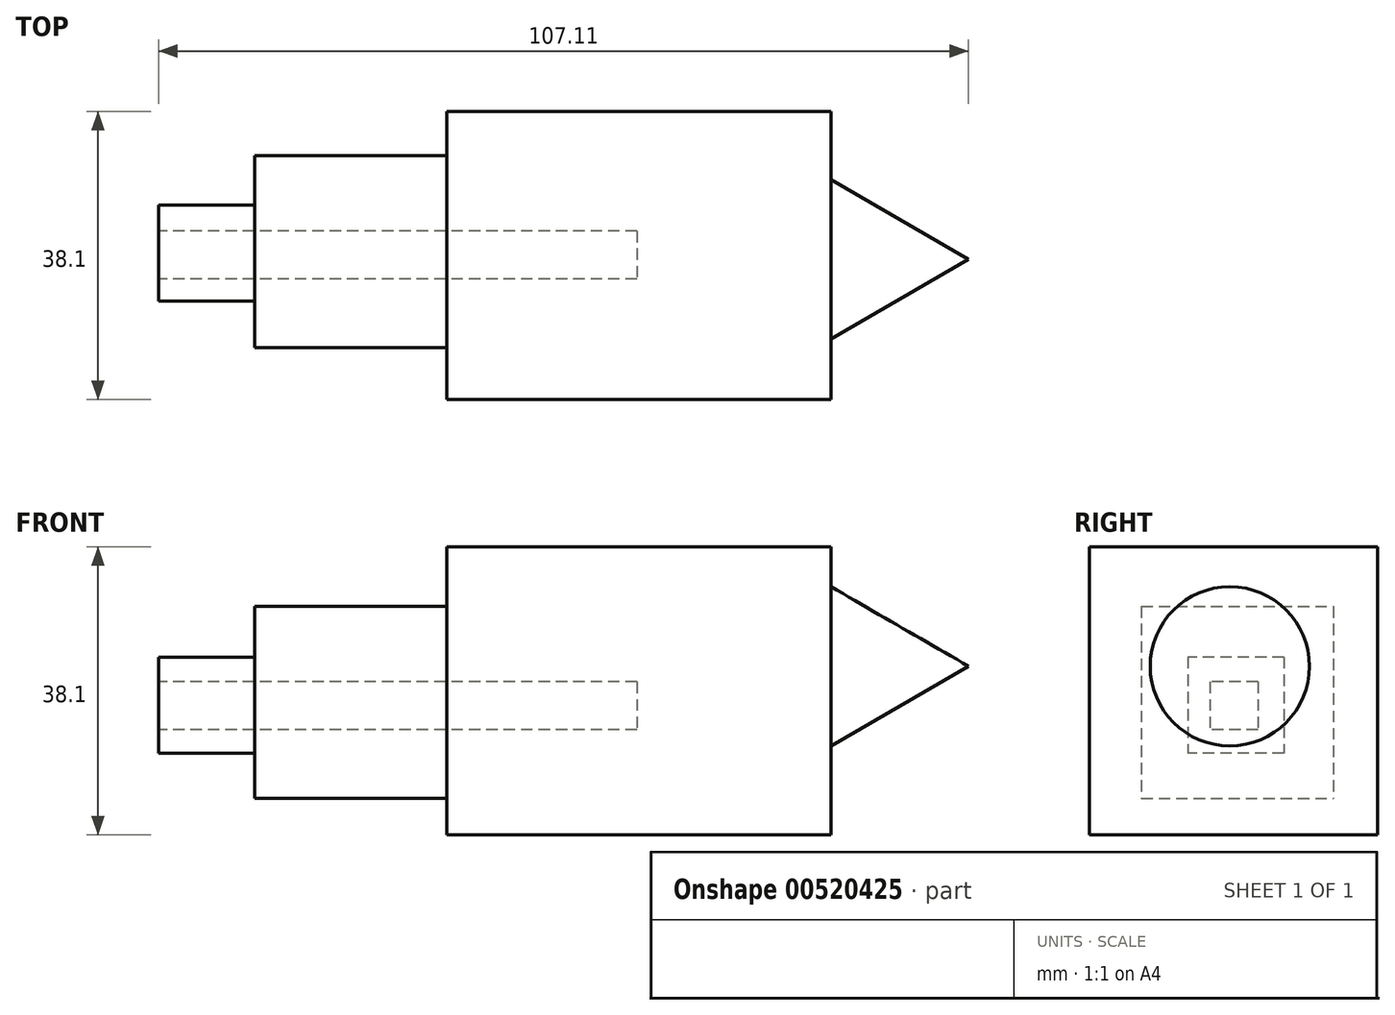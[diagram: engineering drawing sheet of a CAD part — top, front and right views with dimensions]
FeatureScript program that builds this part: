
annotation { "Feature Type Name" : "Feature", "Feature Type Description" : "" }
export const myFeature = defineFeature(function(context is Context, id is Id, definition is map)
    precondition{}
    {
        {
            var Q0;
            Q0=qCreatedBy(makeId("Right.planeOp"),FACE);
            var sketch = newSketch(context, id + "F0", { "sketchPlane" : qUnion([Q0])});
            skLineSegment(sketch, "E0.bottom", {"start": v(-18.66, 15.8) * mm, "end": v(19.44, 15.8) * mm});
            skLineSegment(sketch, "E0.top", {"start": v(-18.66, -22.3) * mm, "end": v(19.44, -22.3) * mm});
            skLineSegment(sketch, "E0.left", {"start": v(-18.66, 15.8) * mm, "end": v(-18.66, -22.3) * mm});
            skLineSegment(sketch, "E0.right", {"start": v(19.44, 15.8) * mm, "end": v(19.44, -22.3) * mm});
            skLineSegment(sketch, "E1.bottom", {"start": v(-12.2, 6.84) * mm, "end": v(13.2, 6.84) * mm});
            skLineSegment(sketch, "E1.top", {"start": v(-12.2, -13.5) * mm, "end": v(13.2, -13.5) * mm});
            skLineSegment(sketch, "E1.left", {"start": v(-12.2, 6.84) * mm, "end": v(-12.2, -13.5) * mm});
            skLineSegment(sketch, "E1.right", {"start": v(13.2, 6.84) * mm, "end": v(13.2, -13.5) * mm});
            skLineSegment(sketch, "E2.bottom", {"start": v(-5.96, 0) * mm, "end": v(6.74, 0) * mm});
            skLineSegment(sketch, "E2.top", {"start": v(-5.96, -6.35) * mm, "end": v(6.74, -6.35) * mm});
            skLineSegment(sketch, "E2.left", {"start": v(-5.96, 0) * mm, "end": v(-5.96, -6.35) * mm});
            skLineSegment(sketch, "E2.right", {"start": v(6.74, 0) * mm, "end": v(6.74, -6.35) * mm});
            skSolve(sketch);
        }
        {
            var Q0;
            Q0=makeQuery(id+"F0.imprint","IMPRINT",FACE,{"disambiguationData":[TD([[makeQuery(id+"F0.imprint","IMPRINT",EDGE,{"derivedFrom":sQuery(id+"F0.wireOp",EDGE,"E0.bottom")}),-1.0]])]});
            extrude(context, id + "F1", {"entities" : qUnion([Q0]), "depth" : 25.4 * mm, "offsetDistance" : 25.4 * mm});
        }
        {
            var Q0;
            Q0=makeQuery(id+"F0.imprint","IMPRINT",FACE,{"disambiguationData":[TD([[makeQuery(id+"F0.imprint","IMPRINT",EDGE,{"derivedFrom":sQuery(id+"F0.wireOp",EDGE,"E0.bottom")}),-1.0]])]});
            var Q1;
            Q1=makeQuery(id+"F0.imprint","IMPRINT",FACE,{"disambiguationData":[TD([[makeQuery(id+"F0.imprint","IMPRINT",EDGE,{"derivedFrom":sQuery(id+"F0.wireOp",EDGE,"E1.bottom")}),-1.0]])]});
            var Q2;
            Q2=makeQuery(id+"F0.imprint","IMPRINT",FACE,{"disambiguationData":[TD([[makeQuery(id+"F0.imprint","IMPRINT",EDGE,{"derivedFrom":sQuery(id+"F0.wireOp",EDGE,"E2.bottom")}),-1.0]])]});
            extrude(context, id + "F2", {"entities" : qUnion([Q0, Q1, Q2]), "operationType" : NewBodyOperationType.ADD, "depth" : 50.8 * mm, "offsetDistance" : 25.4 * mm});
        }
        {
            var Q0;
            Q0=qCreatedBy(makeId("Right.planeOp"),FACE);
            var sketch = newSketch(context, id + "F3", { "sketchPlane" : qUnion([Q0])});
            skLineSegment(sketch, "E3.bottom", {"start": v(-11.8, 7.92) * mm, "end": v(13.6, 7.92) * mm});
            skLineSegment(sketch, "E3.top", {"start": v(-11.8, -17.48) * mm, "end": v(13.6, -17.48) * mm});
            skLineSegment(sketch, "E3.left", {"start": v(-11.8, 7.92) * mm, "end": v(-11.8, -17.48) * mm});
            skLineSegment(sketch, "E3.right", {"start": v(13.6, 7.92) * mm, "end": v(13.6, -17.48) * mm});
            skSolve(sketch);
        }
        {
            var Q0;
            Q0=makeQuery(id+"F3.imprint","IMPRINT",FACE,{"disambiguationData":[TD([[makeQuery(id+"F3.imprint","IMPRINT",EDGE,{"derivedFrom":sQuery(id+"F3.wireOp",EDGE,"E3.bottom")}),-1.0]])]});
            extrude(context, id + "F4", {"entities" : qUnion([Q0]), "operationType" : NewBodyOperationType.ADD, "depth" : 25.4 * mm, "offsetDistance" : 25.4 * mm});
        }
        {
            var Q0;
            Q0=makeQuery(id+"F3.imprint","IMPRINT",FACE,{"disambiguationData":[TD([[makeQuery(id+"F3.imprint","IMPRINT",EDGE,{"derivedFrom":sQuery(id+"F3.wireOp",EDGE,"E3.bottom")}),-1.0]])]});
            extrude(context, id + "F5", {"entities" : qUnion([Q0]), "operationType" : NewBodyOperationType.ADD, "oppositeDirection" : true, "depth" : 25.4 * mm, "offsetDistance" : 25.4 * mm});
        }
        {
            var Q0;
            Q0=makeQuery(id+"F5.opExtrude","CAP_FACE",FACE,{"disambiguationData":[OSD([sQuery(id+"F3.wireOp",EDGE,"E3.bottom"),sQuery(id+"F3.wireOp",EDGE,"E3.top"),sQuery(id+"F3.wireOp",EDGE,"E3.left"),sQuery(id+"F3.wireOp",EDGE,"E3.right")])],"isStart":false});
            var sketch = newSketch(context, id + "F6", { "sketchPlane" : qUnion([Q0])});
            skLineSegment(sketch, "E4.bottom", {"start": v(-7.03, 1.22) * mm, "end": v(5.67, 1.22) * mm});
            skLineSegment(sketch, "E4.top", {"start": v(-7.03, -11.48) * mm, "end": v(5.67, -11.48) * mm});
            skLineSegment(sketch, "E4.left", {"start": v(-7.03, 1.22) * mm, "end": v(-7.03, -11.48) * mm});
            skLineSegment(sketch, "E4.right", {"start": v(5.67, 1.22) * mm, "end": v(5.67, -11.48) * mm});
            skSolve(sketch);
        }
        {
            var Q0;
            Q0=makeQuery(id+"F6.imprint","IMPRINT",FACE,{"disambiguationData":[TD([[makeQuery(id+"F6.imprint","IMPRINT",EDGE,{"derivedFrom":sQuery(id+"F6.wireOp",EDGE,"E4.bottom")}),-1.0]])]});
            extrude(context, id + "F7", {"entities" : qUnion([Q0]), "operationType" : NewBodyOperationType.ADD, "depth" : 12.7 * mm, "offsetDistance" : 25.4 * mm});
        }
        {
            var Q0;
            Q0=makeQuery(id+"F7.opExtrude","CAP_FACE",FACE,{"disambiguationData":[OSD([sQuery(id+"F6.wireOp",EDGE,"E4.bottom"),sQuery(id+"F6.wireOp",EDGE,"E4.top"),sQuery(id+"F6.wireOp",EDGE,"E4.left"),sQuery(id+"F6.wireOp",EDGE,"E4.right")])],"isStart":false});
            var sketch = newSketch(context, id + "F8", { "sketchPlane" : qUnion([Q0])});
            skLineSegment(sketch, "E5.bottom", {"start": v(-3.61, -2.06) * mm, "end": v(2.74, -2.06) * mm});
            skLineSegment(sketch, "E5.top", {"start": v(-3.61, -8.41) * mm, "end": v(2.74, -8.41) * mm});
            skLineSegment(sketch, "E5.left", {"start": v(-3.61, -2.06) * mm, "end": v(-3.61, -8.41) * mm});
            skLineSegment(sketch, "E5.right", {"start": v(2.74, -2.06) * mm, "end": v(2.74, -8.41) * mm});
            skSolve(sketch);
        }
        {
            var Q0;
            Q0=makeQuery(id+"F8.imprint","IMPRINT",FACE,{"disambiguationData":[TD([[makeQuery(id+"F8.imprint","IMPRINT",EDGE,{"derivedFrom":sQuery(id+"F8.wireOp",EDGE,"E5.bottom")}),-1.0]])]});
            extrude(context, id + "F9", {"entities" : qUnion([Q0]), "operationType" : NewBodyOperationType.REMOVE, "oppositeDirection" : true, "depth" : 63.25 * mm, "offsetDistance" : 25.4 * mm});
        }
        {
            var Q0;
            {var subQ0=sQuery(id+"F0.wireOp",EDGE,"E0.right");Q0=makeQuery(id+"F2.boolean.opBoolean","MERGE",FACE,{"derivedFrom":[makeQuery(id+"F1.opExtrude","SWEPT_FACE",FACE,{"disambiguationData":[OSD([subQ0])]}),makeQuery(id+"F2.opExtrude","SWEPT_FACE",FACE,{"disambiguationData":[OSD([subQ0])]})]});}
            var sketch = newSketch(context, id + "F10", { "sketchPlane" : qUnion([Q0])});
            skLineSegment(sketch, "E6", {"start": v(-50.8, 0) * mm, "end": v(-69.01, 0) * mm});
            skLineSegment(sketch, "E7", {"start": v(-69.01, 0) * mm, "end": v(-50.8, -10.53) * mm});
            skLineSegment(sketch, "E8", {"start": v(-50.8, -10.53) * mm, "end": v(-50.8, 0) * mm});
            skSolve(sketch);
        }
        {
            var Q0;
            Q0=makeQuery(id+"F10.imprint","IMPRINT",FACE,{"disambiguationData":[TD([[makeQuery(id+"F10.imprint","IMPRINT",EDGE,{"derivedFrom":sQuery(id+"F10.wireOp",EDGE,"E6")}),1.0]])]});
            var Q1;
            Q1=sQuery(id+"F10.wireOp",EDGE,"E6");
            var Q2;
            Q2=sQuery(id+"F10.wireOp",EDGE,"E6");
            revolve(context, id + "F11", {"entities" : qUnion([Q0]), "surfaceEntities" : qUnion([Q1]), "axis" : qUnion([Q2]), "revolveType" : RevolveType.FULL});
        }
        {
            var Q0;
            Q0=makeQuery(id+"F11.opRevolve","SWEPT_BODY",BODY,{"disambiguationData":[OSD([sQuery(id+"F10.wireOp",EDGE,"E6"),sQuery(id+"F10.wireOp",EDGE,"E7"),sQuery(id+"F10.wireOp",EDGE,"E8")])]});
            transform(context, id + "F12", {"entities" : qUnion([Q0]), "transformType" : TransformType.TRANSLATION_3D, "dx" : 0 * mm, "dy" : -19.56 * mm, "dz" : 0 * mm, "makeCopy" : false});
        }
    });
